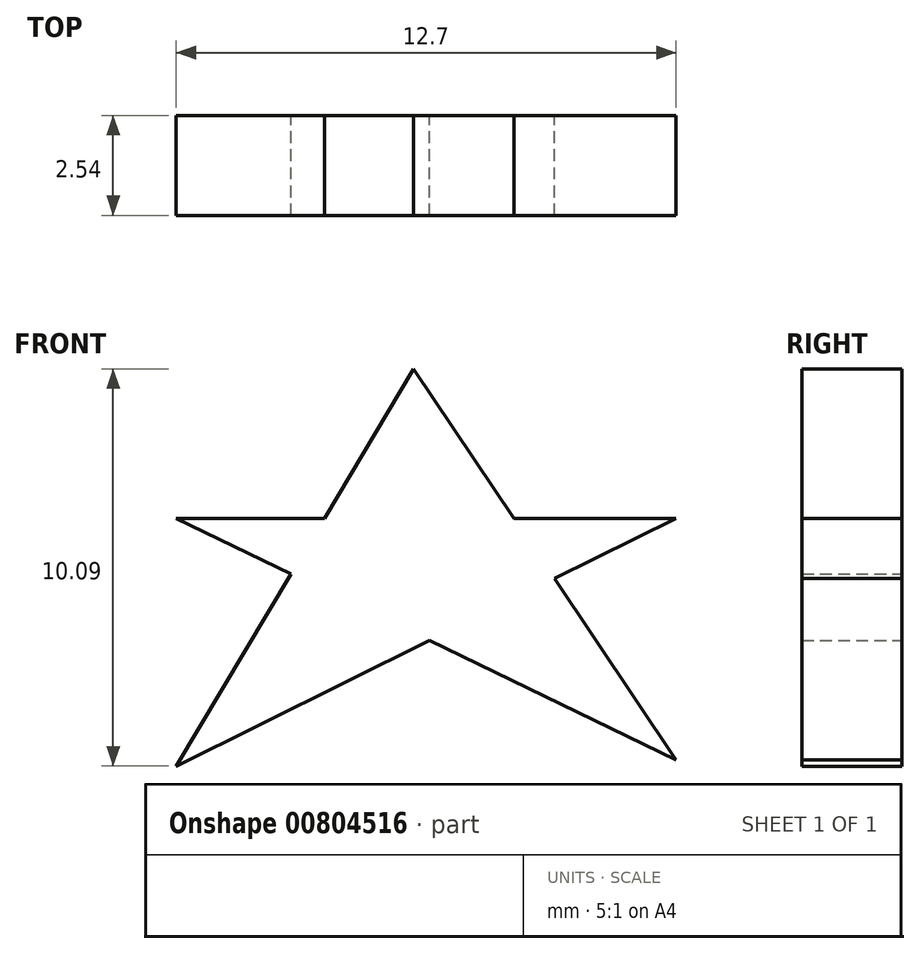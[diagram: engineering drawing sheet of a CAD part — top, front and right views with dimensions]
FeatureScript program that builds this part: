
annotation { "Feature Type Name" : "Feature", "Feature Type Description" : "" }
export const myFeature = defineFeature(function(context is Context, id is Id, definition is map)
    precondition{}
    {
        {
            var Q0;
            Q0=qCreatedBy(makeId("Front.planeOp"),FACE);
            var sketch = newSketch(context, id + "F0", { "sketchPlane" : qUnion([Q0])});
            skLineSegment(sketch, "E0.bottom", {"start": v(0, 0) * mm, "end": v(12.7, 0) * mm, "construction": true});
            skLineSegment(sketch, "E0.top", {"start": v(0, 12.7) * mm, "end": v(12.7, 12.7) * mm, "construction": true});
            skLineSegment(sketch, "E0.left", {"start": v(0, 0) * mm, "end": v(0, 12.7) * mm, "construction": true});
            skLineSegment(sketch, "E0.right", {"start": v(12.7, 0) * mm, "end": v(12.7, 12.7) * mm, "construction": true});
            skLineSegment(sketch, "E1", {"start": v(0, 1.37) * mm, "end": v(6.03, 11.46) * mm, "construction": true});
            skLineSegment(sketch, "E2", {"start": v(6.03, 11.46) * mm, "end": v(12.7, 1.53) * mm, "construction": true});
            skLineSegment(sketch, "E3", {"start": v(12.7, 1.53) * mm, "end": v(0, 7.67) * mm, "construction": true});
            skLineSegment(sketch, "E4", {"start": v(0, 7.67) * mm, "end": v(12.7, 7.67) * mm, "construction": true});
            skLineSegment(sketch, "E5", {"start": v(12.7, 7.67) * mm, "end": v(0, 1.37) * mm, "construction": true});
            skLineSegment(sketch, "E6", {"start": v(0, 1.37) * mm, "end": v(6.03, 11.46) * mm});
            skLineSegment(sketch, "E7", {"start": v(12.7, 1.53) * mm, "end": v(6.03, 11.46) * mm});
            skLineSegment(sketch, "E8", {"start": v(12.7, 1.53) * mm, "end": v(0, 7.67) * mm});
            skLineSegment(sketch, "E9", {"start": v(0, 7.67) * mm, "end": v(12.7, 7.67) * mm});
            skLineSegment(sketch, "E10", {"start": v(12.7, 7.67) * mm, "end": v(0, 1.37) * mm});
            skSolve(sketch);
        }
        {
            var Q0;
            Q0 = qSketchRegion(id + "F0", true);
            extrude(context, id + "F1", {"entities" : qUnion([Q0]), "depth" : 2.54 * mm, "offsetDistance" : 25.4 * mm});
        }
    });
